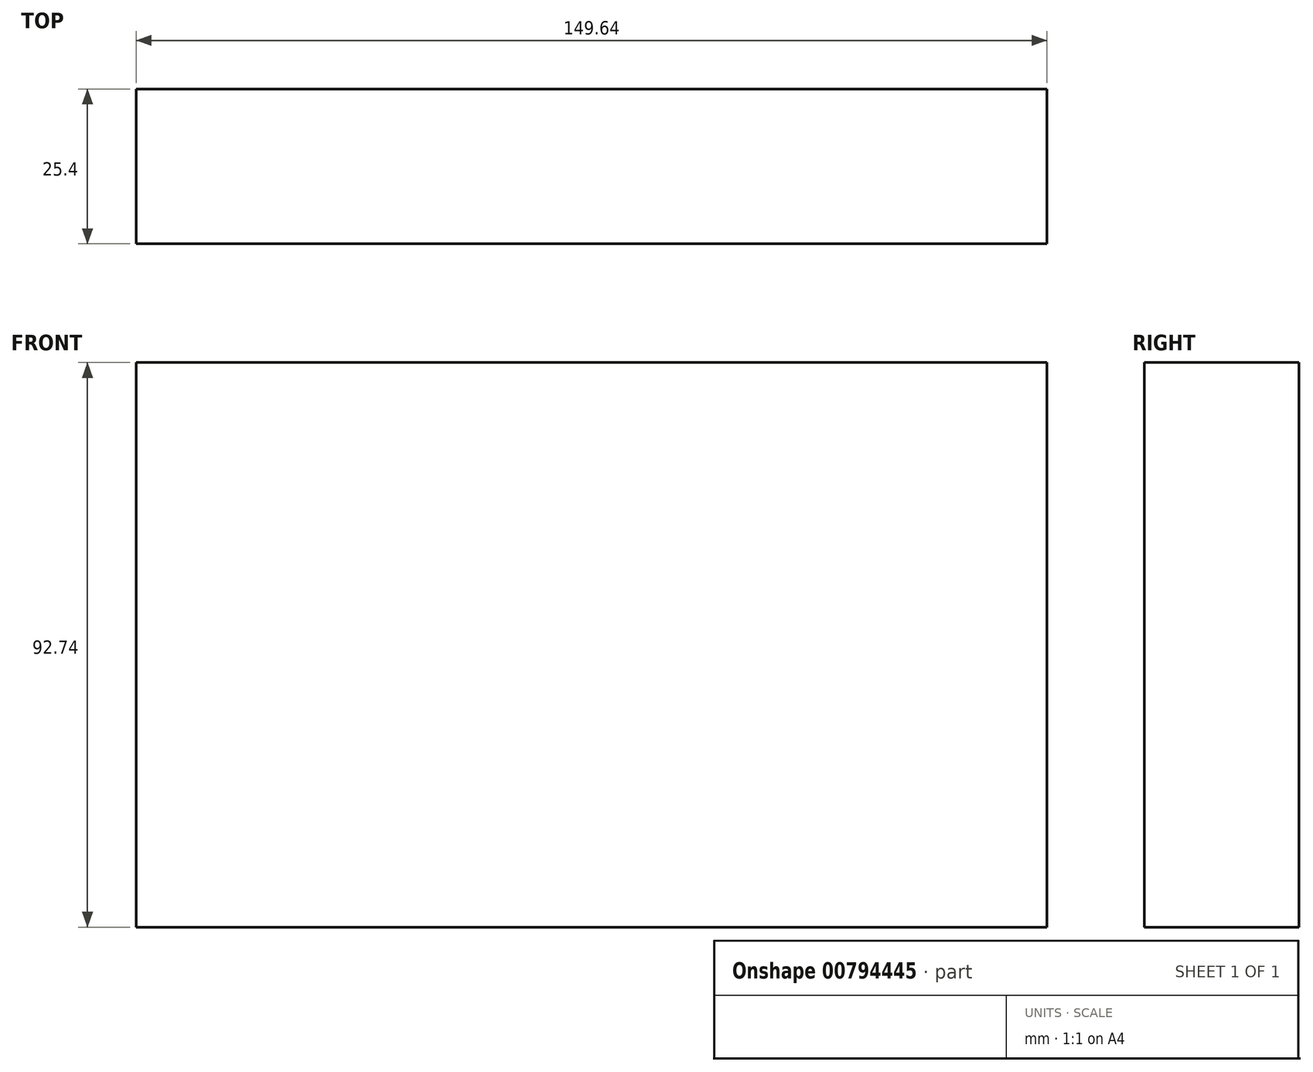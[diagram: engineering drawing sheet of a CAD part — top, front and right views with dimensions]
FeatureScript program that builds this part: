
annotation { "Feature Type Name" : "Feature", "Feature Type Description" : "" }
export const myFeature = defineFeature(function(context is Context, id is Id, definition is map)
    precondition{}
    {
        {
            var Q0;
            Q0=qCreatedBy(makeId("Front.planeOp"),FACE);
            var sketch = newSketch(context, id + "F0", { "sketchPlane" : qUnion([Q0])});
            skLineSegment(sketch, "E0", {"start": v(-25.94, 36.47) * mm, "end": v(38.51, 36.47) * mm});
            skLineSegment(sketch, "E1", {"start": v(-25.94, 36.47) * mm, "end": v(-75.3, 36.47) * mm});
            skLineSegment(sketch, "E2", {"start": v(-75.3, 36.47) * mm, "end": v(74.35, 36.47) * mm});
            skLineSegment(sketch, "E3", {"start": v(74.35, 36.47) * mm, "end": v(74.35, -27.35) * mm});
            skLineSegment(sketch, "E4", {"start": v(74.35, -27.35) * mm, "end": v(-75.3, -27.35) * mm});
            skLineSegment(sketch, "E5", {"start": v(-75.3, -27.35) * mm, "end": v(-75.3, 36.47) * mm});
            skLineSegment(sketch, "E6", {"start": v(-75.3, 36.47) * mm, "end": v(-33.8, -27.35) * mm});
            skLineSegment(sketch, "E7", {"start": v(-33.8, -27.35) * mm, "end": v(-25.94, 36.47) * mm});
            skLineSegment(sketch, "E8", {"start": v(-25.94, 36.47) * mm, "end": v(10.53, -27.35) * mm});
            skLineSegment(sketch, "E9", {"start": v(10.53, -27.35) * mm, "end": v(38.51, 36.47) * mm});
            skLineSegment(sketch, "E10", {"start": v(38.51, 36.47) * mm, "end": v(74.35, -27.35) * mm});
            skLineSegment(sketch, "E11", {"start": v(-75.3, -27.35) * mm, "end": v(-75.3, -56.27) * mm});
            skLineSegment(sketch, "E12", {"start": v(-75.3, -56.27) * mm, "end": v(-43.54, -56.27) * mm});
            skLineSegment(sketch, "E13", {"start": v(-43.54, -56.27) * mm, "end": v(74.35, -56.27) * mm});
            skLineSegment(sketch, "E14", {"start": v(74.35, -56.27) * mm, "end": v(74.35, -20.75) * mm});
            skLineSegment(sketch, "E15", {"start": v(-75.3, 36.47) * mm, "end": v(-75.3, 56.27) * mm});
            skLineSegment(sketch, "E16", {"start": v(-75.3, 56.27) * mm, "end": v(56.43, 56.27) * mm});
            skLineSegment(sketch, "E17", {"start": v(56.43, 56.27) * mm, "end": v(79.7, 56.27) * mm});
            skSolve(sketch);
        }
        {
            var Q0;
            {var subQ0=sQuery(id+"F0.wireOp",EDGE,"E7");Q0=makeQuery(id+"F0.imprint","IMPRINT",FACE,{"disambiguationData":[TD([[makeQuery(id+"F0.imprint","IMPRINT",EDGE,{"derivedFrom":subQ0}),-1.0]])]});}
            var Q1;
            {var subQ0=sQuery(id+"F0.wireOp",EDGE,"E6");Q1=makeQuery(id+"F0.imprint","IMPRINT",FACE,{"disambiguationData":[TD([[makeQuery(id+"F0.imprint","IMPRINT",EDGE,{"derivedFrom":subQ0}),1.0]])]});}
            var Q2;
            {var subQ0=sQuery(id+"F0.wireOp",EDGE,"E5");Q2=makeQuery(id+"F0.imprint","IMPRINT",FACE,{"disambiguationData":[TD([[makeQuery(id+"F0.imprint","IMPRINT",EDGE,{"derivedFrom":subQ0}),-1.0]])]});}
            var Q3;
            {var subQ0=sQuery(id+"F0.wireOp",EDGE,"E11");Q3=makeQuery(id+"F0.imprint","IMPRINT",FACE,{"disambiguationData":[TD([[makeQuery(id+"F0.imprint","IMPRINT",EDGE,{"derivedFrom":subQ0}),1.0]])]});}
            var Q4;
            {var subQ2=sQuery(id+"F0.wireOp",EDGE,"E9");Q4=makeQuery(id+"F0.imprint","IMPRINT",FACE,{"disambiguationData":[TD([[makeQuery(id+"F0.imprint","IMPRINT",EDGE,{"derivedFrom":subQ2}),-1.0]])]});}
            var Q5;
            {var subQ0=sQuery(id+"F0.wireOp",EDGE,"E3");Q5=makeQuery(id+"F0.imprint","IMPRINT",FACE,{"disambiguationData":[TD([[makeQuery(id+"F0.imprint","IMPRINT",EDGE,{"derivedFrom":subQ0}),-1.0]])]});}
            var Q6;
            {var subQ0=sQuery(id+"F0.wireOp",EDGE,"E8");Q6=makeQuery(id+"F0.imprint","IMPRINT",FACE,{"disambiguationData":[TD([[makeQuery(id+"F0.imprint","IMPRINT",EDGE,{"derivedFrom":subQ0}),1.0]])]});}
            extrude(context, id + "F1", {"entities" : qUnion([Q0, Q1, Q2, Q3, Q4, Q5, Q6]), "depth" : 25.4 * mm, "offsetDistance" : 25.4 * mm});
        }
    });
